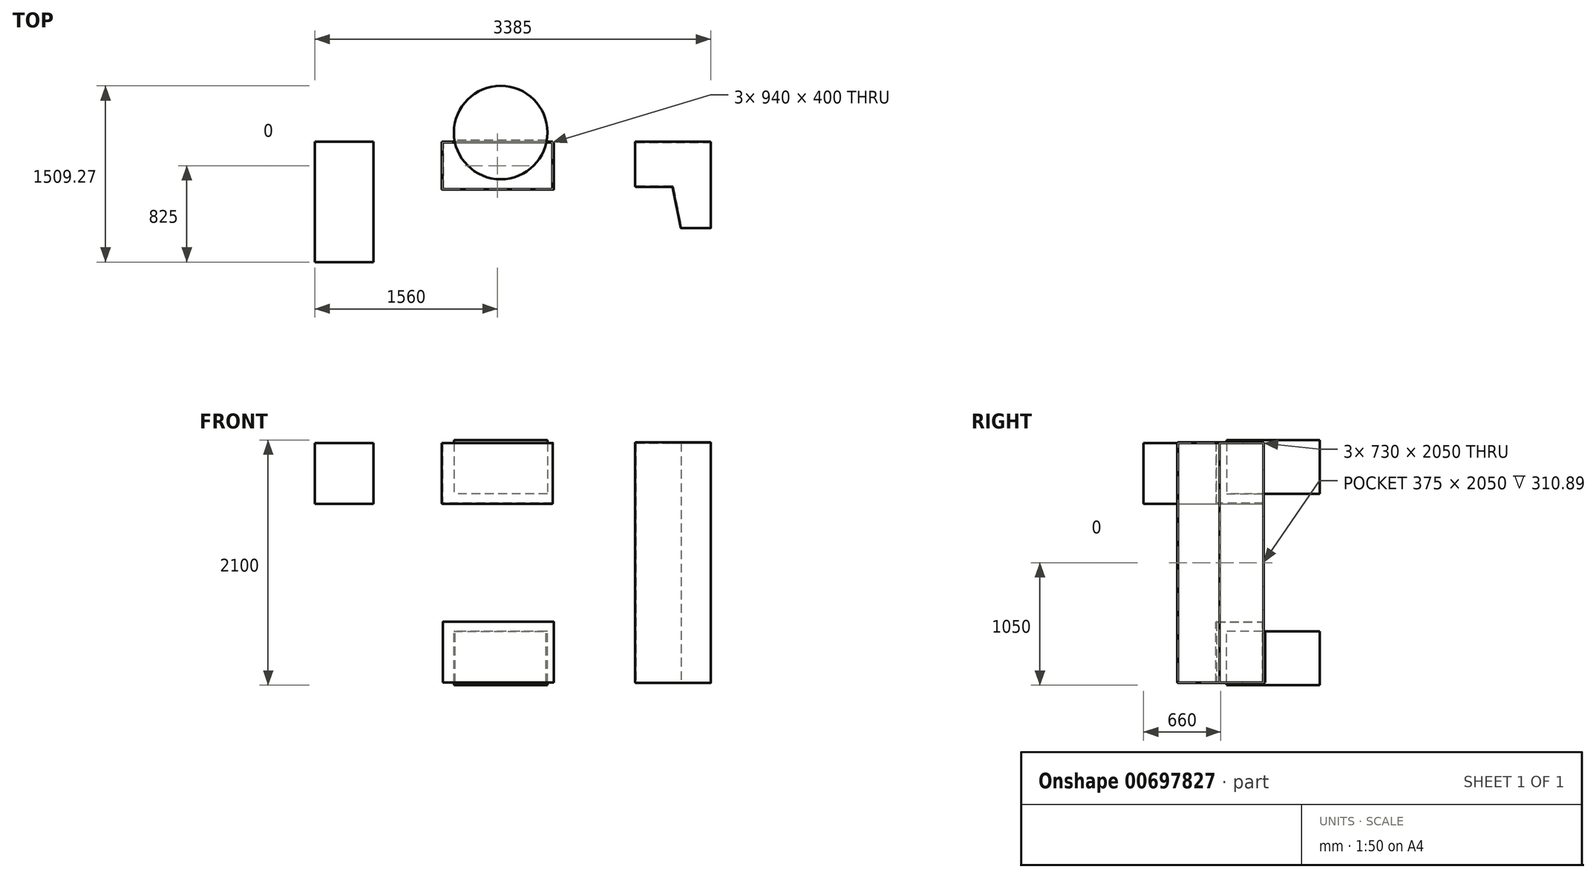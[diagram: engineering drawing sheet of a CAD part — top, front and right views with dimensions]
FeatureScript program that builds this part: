
annotation { "Feature Type Name" : "Feature", "Feature Type Description" : "" }
export const myFeature = defineFeature(function(context is Context, id is Id, definition is map)
    precondition{}
    {
        {
            var Q0;
            Q0=qCreatedBy(makeId("Front.planeOp"),FACE);
            var sketch = newSketch(context, id + "F0", { "sketchPlane" : qUnion([Q0])});
            skLineSegment(sketch, "E0.bottom", {"start": v(-3963.56, -1370.66) * mm, "end": v(966.44, -1370.66) * mm});
            skLineSegment(sketch, "E0.top", {"start": v(-3963.56, -3430.66) * mm, "end": v(966.44, -3430.66) * mm});
            skLineSegment(sketch, "E0.left", {"start": v(-3963.56, -1370.66) * mm, "end": v(-3963.56, -3430.66) * mm});
            skLineSegment(sketch, "E0.right", {"start": v(966.44, -1370.66) * mm, "end": v(966.44, -3430.66) * mm});
            skLineSegment(sketch, "E1.bottom", {"start": v(961.44, -1375.66) * mm, "end": v(316.44, -1375.66) * mm});
            skLineSegment(sketch, "E1.top", {"start": v(961.44, -3425.66) * mm, "end": v(316.44, -3425.66) * mm});
            skLineSegment(sketch, "E1.left", {"start": v(961.44, -1375.66) * mm, "end": v(961.44, -3425.66) * mm});
            skLineSegment(sketch, "E1.right", {"start": v(316.44, -1375.66) * mm, "end": v(316.44, -3425.66) * mm});
            skLineSegment(sketch, "E2.bottom", {"start": v(-383.56, -1375.66) * mm, "end": v(-1333.56, -1375.66) * mm});
            skLineSegment(sketch, "E2.top", {"start": v(-383.56, -1895.66) * mm, "end": v(-1333.56, -1895.66) * mm});
            skLineSegment(sketch, "E2.left", {"start": v(-383.56, -1375.66) * mm, "end": v(-383.56, -1895.66) * mm});
            skLineSegment(sketch, "E2.right", {"start": v(-1333.56, -1375.66) * mm, "end": v(-1333.56, -1895.66) * mm});
            skLineSegment(sketch, "E3.bottom", {"start": v(-373.56, -3425.66) * mm, "end": v(-1323.56, -3425.66) * mm});
            skLineSegment(sketch, "E3.top", {"start": v(-373.56, -2905.66) * mm, "end": v(-1323.56, -2905.66) * mm});
            skLineSegment(sketch, "E3.left", {"start": v(-373.56, -3425.66) * mm, "end": v(-373.56, -2905.66) * mm});
            skLineSegment(sketch, "E3.right", {"start": v(-1323.56, -3425.66) * mm, "end": v(-1323.56, -2905.66) * mm});
            skLineSegment(sketch, "E4.bottom", {"start": v(-2000.5, -2776.88) * mm, "end": v(-2480.02, -2776.88) * mm});
            skLineSegment(sketch, "E4.top", {"start": v(-2000.5, -3193.73) * mm, "end": v(-2480.02, -3193.73) * mm});
            skLineSegment(sketch, "E4.left", {"start": v(-2000.5, -2776.88) * mm, "end": v(-2000.5, -3193.73) * mm});
            skLineSegment(sketch, "E4.right", {"start": v(-2480.02, -2776.88) * mm, "end": v(-2480.02, -3193.73) * mm});
            skLineSegment(sketch, "E5.bottom", {"start": v(-1918.56, -1375.66) * mm, "end": v(-2418.56, -1375.66) * mm});
            skLineSegment(sketch, "E5.top", {"start": v(-1918.56, -1895.66) * mm, "end": v(-2418.56, -1895.66) * mm});
            skLineSegment(sketch, "E5.left", {"start": v(-1918.56, -1375.66) * mm, "end": v(-1918.56, -1895.66) * mm});
            skLineSegment(sketch, "E5.right", {"start": v(-2418.56, -1375.66) * mm, "end": v(-2418.56, -1895.66) * mm});
            skLineSegment(sketch, "E6.bottom", {"start": v(-378.56, -1375.66) * mm, "end": v(311.44, -1375.66) * mm});
            skLineSegment(sketch, "E6.top", {"start": v(-378.56, -1895.66) * mm, "end": v(311.44, -1895.66) * mm});
            skLineSegment(sketch, "E6.left", {"start": v(-378.56, -1375.66) * mm, "end": v(-378.56, -1895.66) * mm});
            skLineSegment(sketch, "E6.right", {"start": v(311.44, -1375.66) * mm, "end": v(311.44, -1895.66) * mm});
            skPoint(sketch, "E7.firstSnap0", {"position": v(311.44, -1635.66) * mm});
            skText(sketch, "E8", { "text": "12\n", "fontName": "OpenSans-Regular.ttf"});
            skPoint(sketch, "E9", {"position": v(961.44, -2400.66) * mm});
            skPoint(sketch, "E10", {"position": v(966.44, -2400.66) * mm});
            skLineSegment(sketch, "E11", {"start": v(-6385, -1996.01) * mm, "end": v(-5740, -1996.01) * mm});
            skLineSegment(sketch, "E12", {"start": v(-5740, -1996.01) * mm, "end": v(-5740, -1256.01) * mm});
            skLineSegment(sketch, "E13", {"start": v(-5740, -1256.01) * mm, "end": v(-5995, -1256.01) * mm});
            skLineSegment(sketch, "E14", {"start": v(-5995, -1256.01) * mm, "end": v(-6065, -1611.01) * mm});
            skLineSegment(sketch, "E15", {"start": v(-6065, -1611.01) * mm, "end": v(-6385, -1611.01) * mm});
            skLineSegment(sketch, "E16", {"start": v(-6385, -1611.01) * mm, "end": v(-6385, -1996.01) * mm});
            const initialGuessF0  = {"E8": [1.74472, -2.01492, 1, 0, 0.18388]};
            skSetInitialGuess(sketch, initialGuessF0);
            skSolve(sketch);
        }
        {
            var Q0;
            Q0=makeQuery(id+"F0.imprint","IMPRINT",FACE,{"disambiguationData":[TD([[makeQuery(id+"F0.imprint","IMPRINT",EDGE,{"derivedFrom":sQuery(id+"F0.wireOp",EDGE,"E5.bottom")}),1.0]])]});
            extrude(context, id + "F1", {"entities" : qUnion([Q0]), "depth" : 1030 * mm, "offsetDistance" : 25 * mm});
        }
        {
            var Q0;
            Q0=makeQuery(id+"F0.imprint","IMPRINT",FACE,{"disambiguationData":[TD([[makeQuery(id+"F0.imprint","IMPRINT",EDGE,{"derivedFrom":sQuery(id+"F0.wireOp",EDGE,"E2.bottom")}),1.0]])]});
            var Q1;
            Q1=makeQuery(id+"F0.imprint","IMPRINT",FACE,{"disambiguationData":[TD([[makeQuery(id+"F0.imprint","IMPRINT",EDGE,{"derivedFrom":sQuery(id+"F0.wireOp",EDGE,"E3.bottom")}),-1.0]])]});
            extrude(context, id + "F2", {"entities" : qUnion([Q0, Q1]), "depth" : 410 * mm, "offsetDistance" : 25 * mm});
        }
        {
            var Q0;
            Q0=sQuery(id+"F0.wireOp",EDGE,"E0.top");
            cPlane(context, id + "F3", {"entities" : qUnion([Q0]), "cplaneType" : CPlaneType.LINE_ANGLE, "offset" : 3442 * mm, "angle" : 90 * degree, "oppositeDirection" : true, "width" : 150 * mm, "height" : 150 * mm});
        }
        {
            var Q0;
            Q0=qCreatedBy(id+"F3.planeOp",FACE);
            var sketch = newSketch(context, id + "F4", { "sketchPlane" : qUnion([Q0])});
            skLineSegment(sketch, "E17", {"start": v(321.44, 0) * mm, "end": v(966.44, 0) * mm});
            skLineSegment(sketch, "E18", {"start": v(966.44, 0) * mm, "end": v(966.44, 740) * mm});
            skLineSegment(sketch, "E19", {"start": v(966.44, 740) * mm, "end": v(711.44, 740) * mm});
            skLineSegment(sketch, "E20", {"start": v(711.44, 740) * mm, "end": v(641.44, 385) * mm});
            skLineSegment(sketch, "E21", {"start": v(641.44, 385) * mm, "end": v(321.44, 385) * mm});
            skLineSegment(sketch, "E22", {"start": v(321.44, 385) * mm, "end": v(321.44, 0) * mm});
            skSolve(sketch);
        }
        {
            var Q0;
            Q0 = qSketchRegion(id + "F4", true);
            extrude(context, id + "F5", {"entities" : qUnion([Q0]), "oppositeDirection" : true, "depth" : 2060 * mm, "offsetDistance" : 25 * mm});
        }
        {
            var Q0;
            Q0=makeQuery(id+"F2.opExtrude","CAP_EDGE",EDGE,{"disambiguationData":[OSD([sQuery(id+"F0.wireOp",EDGE,"E2.right")])],"isStart":false});
            var Q1;
            Q1=makeQuery(id+"F2.opExtrude","CAP_EDGE",EDGE,{"disambiguationData":[OSD([sQuery(id+"F0.wireOp",EDGE,"E2.left")])],"isStart":false});
            var Q2;
            Q2=makeQuery(id+"F2.opExtrude","SWEPT_EDGE",EDGE,{"disambiguationData":[OSD([sQuery(id+"F0.wireOp",EDGE,"E2.top"),sQuery(id+"F0.wireOp",EDGE,"E2.right")])]});
            var Q3;
            Q3=makeQuery(id+"F2.opExtrude","CAP_EDGE",EDGE,{"disambiguationData":[OSD([sQuery(id+"F0.wireOp",EDGE,"E2.top")])],"isStart":false});
            var Q4;
            Q4=makeQuery(id+"F2.opExtrude","SWEPT_EDGE",EDGE,{"disambiguationData":[OSD([sQuery(id+"F0.wireOp",EDGE,"E2.top"),sQuery(id+"F0.wireOp",EDGE,"E2.left")])]});
            var Q5;
            Q5=makeQuery(id+"F5.opExtrude","SWEPT_EDGE",EDGE,{"disambiguationData":[OSD([sQuery(id+"F4.wireOp",EDGE,"E21"),sQuery(id+"F4.wireOp",EDGE,"E22")])]});
            var Q6;
            Q6=makeQuery(id+"F5.opExtrude","CAP_EDGE",EDGE,{"disambiguationData":[OSD([sQuery(id+"F4.wireOp",EDGE,"E22")])],"isStart":false});
            var Q7;
            Q7=makeQuery(id+"F5.opExtrude","CAP_EDGE",EDGE,{"disambiguationData":[OSD([sQuery(id+"F4.wireOp",EDGE,"E21")])],"isStart":false});
            var Q8;
            Q8=makeQuery(id+"F5.opExtrude","CAP_EDGE",EDGE,{"disambiguationData":[OSD([sQuery(id+"F4.wireOp",EDGE,"E20")])],"isStart":false});
            var Q9;
            Q9=makeQuery(id+"F5.opExtrude","CAP_EDGE",EDGE,{"disambiguationData":[OSD([sQuery(id+"F4.wireOp",EDGE,"E19")])],"isStart":false});
            var Q10;
            Q10=makeQuery(id+"F5.opExtrude","SWEPT_EDGE",EDGE,{"disambiguationData":[OSD([sQuery(id+"F4.wireOp",EDGE,"E19"),sQuery(id+"F4.wireOp",EDGE,"E20")])]});
            var Q11;
            Q11=makeQuery(id+"F5.opExtrude","CAP_EDGE",EDGE,{"disambiguationData":[OSD([sQuery(id+"F4.wireOp",EDGE,"E19")])],"isStart":true});
            var Q12;
            Q12=makeQuery(id+"F5.opExtrude","CAP_EDGE",EDGE,{"disambiguationData":[OSD([sQuery(id+"F4.wireOp",EDGE,"E20")])],"isStart":true});
            var Q13;
            Q13=makeQuery(id+"F5.opExtrude","CAP_EDGE",EDGE,{"disambiguationData":[OSD([sQuery(id+"F4.wireOp",EDGE,"E21")])],"isStart":true});
            var Q14;
            Q14=makeQuery(id+"F5.opExtrude","CAP_EDGE",EDGE,{"disambiguationData":[OSD([sQuery(id+"F4.wireOp",EDGE,"E22")])],"isStart":true});
            var Q15;
            Q15=makeQuery(id+"F2.opExtrude","CAP_EDGE",EDGE,{"disambiguationData":[OSD([sQuery(id+"F0.wireOp",EDGE,"E3.right")])],"isStart":false});
            var Q16;
            Q16=makeQuery(id+"F2.opExtrude","CAP_EDGE",EDGE,{"disambiguationData":[OSD([sQuery(id+"F0.wireOp",EDGE,"E3.top")])],"isStart":false});
            var Q17;
            Q17=makeQuery(id+"F2.opExtrude","CAP_EDGE",EDGE,{"disambiguationData":[OSD([sQuery(id+"F0.wireOp",EDGE,"E3.left")])],"isStart":false});
            var Q18;
            Q18=makeQuery(id+"F2.opExtrude","SWEPT_EDGE",EDGE,{"disambiguationData":[OSD([sQuery(id+"F0.wireOp",EDGE,"E3.top"),sQuery(id+"F0.wireOp",EDGE,"E3.left")])]});
            var Q19;
            Q19=makeQuery(id+"F2.opExtrude","SWEPT_EDGE",EDGE,{"disambiguationData":[OSD([sQuery(id+"F0.wireOp",EDGE,"E3.top"),sQuery(id+"F0.wireOp",EDGE,"E3.right")])]});
            var Q20;
            Q20=makeQuery(id+"F5.opExtrude","SWEPT_EDGE",EDGE,{"disambiguationData":[OSD([sQuery(id+"F4.wireOp",EDGE,"E20"),sQuery(id+"F4.wireOp",EDGE,"E21")])]});
            fillet(context, id + "F6", {"entities" : qUnion([Q0, Q1, Q2, Q3, Q4, Q5, Q6, Q7, Q8, Q9, Q10, Q11, Q12, Q13, Q14, Q15, Q16, Q17, Q18, Q19, Q20]), "radius" : 5 * mm, "tangentPropagation" : true, "allowEdgeOverflow" : false});
        }
        {
            var Q0;
            Q0=makeQuery(id+"F2.opExtrude","SWEPT_FACE",FACE,{"disambiguationData":[OSD([sQuery(id+"F0.wireOp",EDGE,"E3.bottom")])]});
            var Q1;
            Q1=makeQuery(id+"F2.opExtrude","SWEPT_FACE",FACE,{"disambiguationData":[OSD([sQuery(id+"F0.wireOp",EDGE,"E2.bottom")])]});
            shell(context, id + "F7", {"entities" : qUnion([Q0, Q1]), "thickness" : 5 * mm});
        }
        {
            var Q0;
            Q0=makeQuery(id+"F5.opExtrude","SWEPT_FACE",FACE,{"disambiguationData":[OSD([sQuery(id+"F4.wireOp",EDGE,"E18")])]});
            shell(context, id + "F8", {"entities" : qUnion([Q0]), "thickness" : 5 * mm});
        }
        {
            var Q0;
            Q0=makeQuery(id+"F7.opShell","OFFSET_FACE",FACE,{"disambiguationData":[OSD([sQuery(id+"F0.wireOp",EDGE,"E3.top")])]});
            var sketch = newSketch(context, id + "F9", { "sketchPlane" : qUnion([Q0])});
            skCircle(sketch, "E23", {"center": v(-829.9, -79.27) * mm, "radius": 400 * mm});
            skSolve(sketch);
        }
        {
            var Q0;
            Q0 = qSketchRegion(id + "F9", true);
            extrude(context, id + "F10", {"entities" : qUnion([Q0]), "operationType" : NewBodyOperationType.ADD, "depth" : 540 * mm, "offsetDistance" : 25 * mm, "hasSecondDirection" : true, "secondDirectionOppositeDirection" : false, "secondDirectionDepth" : 79 * mm});
        }
        {
            var Q0;
            Q0=makeQuery(id+"F0.imprint","IMPRINT",FACE,{"disambiguationData":[TD([[makeQuery(id+"F0.imprint","IMPRINT",EDGE,{"derivedFrom":sQuery(id+"F0.wireOp",EDGE,"E3.bottom")}),-1.0]])]});
            extrude(context, id + "F11", {"entities" : qUnion([Q0]), "operationType" : NewBodyOperationType.REMOVE, "oppositeDirection" : true, "depth" : 25 * mm, "offsetDistance" : 25 * mm, "symmetric" : true});
        }
        {
            var Q0;
            Q0=makeQuery(id+"F7.opShell","OFFSET_FACE",FACE,{"disambiguationData":[OSD([sQuery(id+"F0.wireOp",EDGE,"E2.top")])]});
            var sketch = newSketch(context, id + "F12", { "sketchPlane" : qUnion([Q0])});
            skCircle(sketch, "E24", {"center": v(-829.9, 79.27) * mm, "radius": 400 * mm});
            skSolve(sketch);
        }
        {
            var Q0;
            {var subQ0=sQuery(id+"F12.wireOp",EDGE,"E24");var subQ1=makeQuery(id+"F7.opShell","OFFSET_EDGE",EDGE,{"disambiguationData":[OSD([sQuery(id+"F0.wireOp",EDGE,"E2.top")])]});var subQ2=makeQuery(id+"F12.imprint","INTERSECT",VERTEX,{"disambiguationData":[OD(0.0)],"derivedFrom":[subQ1,subQ0]});Q0=makeQuery(id+"F12.imprint","IMPRINT",FACE,{"disambiguationData":[TD([[makeQuery(id+"F12.imprint","IMPRINT",EDGE,{"disambiguationData":[TD([[subQ2,-1.0]])],"derivedFrom":subQ0}),1.0]])]});}
            var Q1;
            {var subQ0=sQuery(id+"F12.wireOp",EDGE,"E24");var subQ1=makeQuery(id+"F7.opShell","OFFSET_EDGE",EDGE,{"disambiguationData":[OSD([sQuery(id+"F0.wireOp",EDGE,"E2.top")])]});var subQ2=makeQuery(id+"F12.imprint","INTERSECT",VERTEX,{"disambiguationData":[OD(0.0)],"derivedFrom":[subQ1,subQ0]});Q1=makeQuery(id+"F12.imprint","IMPRINT",FACE,{"disambiguationData":[TD([[makeQuery(id+"F12.imprint","IMPRINT",EDGE,{"disambiguationData":[TD([[subQ2,1.0]])],"derivedFrom":subQ0}),1.0]])]});}
            extrude(context, id + "F13", {"entities" : qUnion([Q0, Q1]), "depth" : 540 * mm, "offsetDistance" : 25 * mm, "hasSecondDirection" : true, "secondDirectionOppositeDirection" : false, "secondDirectionDepth" : 79 * mm});
        }
    });
